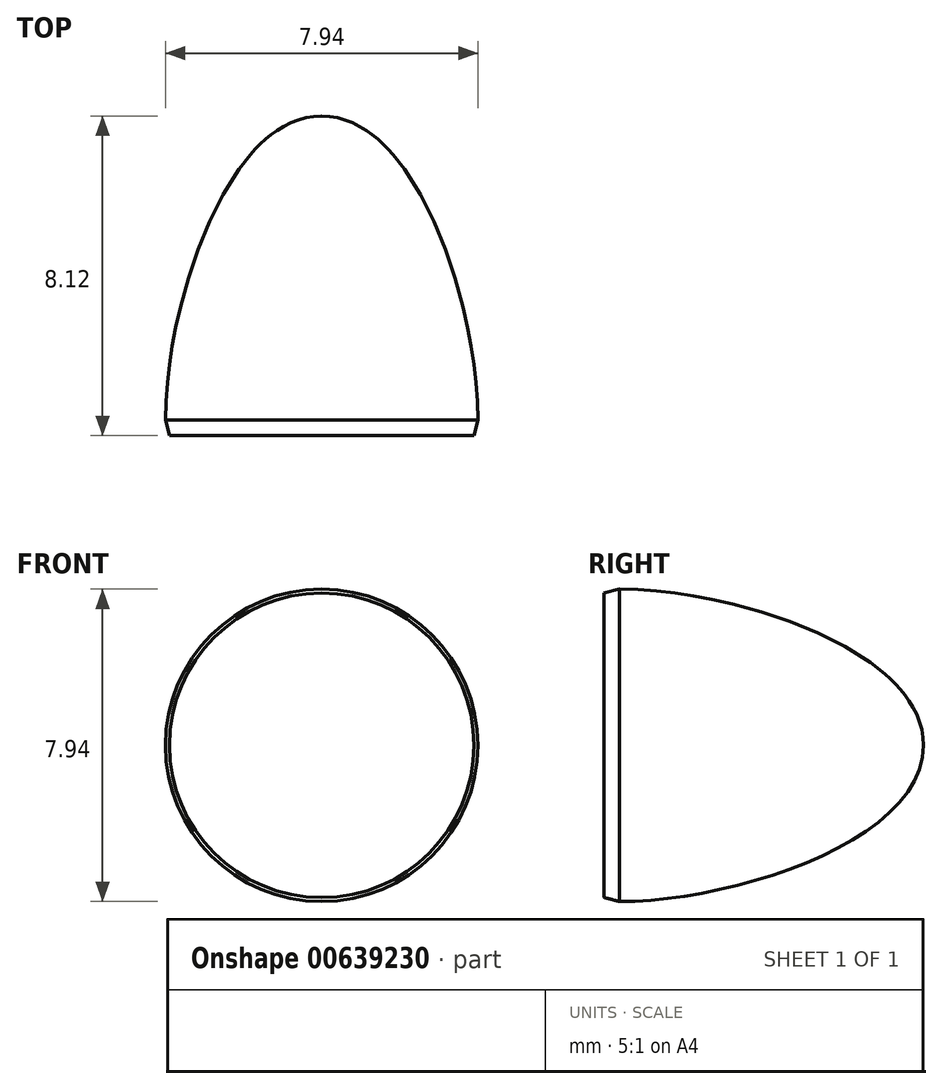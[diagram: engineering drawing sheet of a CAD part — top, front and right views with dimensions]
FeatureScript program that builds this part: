
annotation { "Feature Type Name" : "Feature", "Feature Type Description" : "" }
export const myFeature = defineFeature(function(context is Context, id is Id, definition is map)
    precondition{}
    {
        {
            var Q0;
            Q0=qCreatedBy(makeId("Right.planeOp"),FACE);
            var sketch = newSketch(context, id + "F0", { "sketchPlane" : qUnion([Q0])});
            skLineSegment(sketch, "E0", {"start": v(-7.46, 0) * mm, "end": v(7.72, 0) * mm, "construction": true});
            skLineSegment(sketch, "E1", {"start": v(0, 0) * mm, "end": v(0, -3.87) * mm, "construction": true});
            skPoint(sketch, "E2.orphan", {"position": v(0, 5.07) * mm});
            skFitSpline(sketch, "E3", {"points": [v(0, -3.97) * mm, v(7.72, 0) * mm], "startDerivative": vector(8.68, 0) * mm, "endDerivative": vector(0, 7.29) * mm});
            skLineSegment(sketch, "E4", {"start": v(7.72, 0) * mm, "end": v(7.72, 4.51) * mm, "construction": true});
            skLineSegment(sketch, "E5", {"start": v(0, -3.97) * mm, "end": v(-9.45, -3.97) * mm, "construction": true});
            skLineSegment(sketch, "E6", {"start": v(-0.4, -3.87) * mm, "end": v(-0.4, 0) * mm});
            skLineSegment(sketch, "E7", {"start": v(-0.4, 0) * mm, "end": v(7.72, 0) * mm});
            skLineSegment(sketch, "E8", {"start": v(0, -3.97) * mm, "end": v(-0.4, -3.87) * mm});
            skSolve(sketch);
        }
        {
            var Q0;
            Q0=makeQuery(id+"F0.imprint","IMPRINT",FACE,{"disambiguationData":[TD([[makeQuery(id+"F0.imprint","IMPRINT",EDGE,{"derivedFrom":sQuery(id+"F0.wireOp",EDGE,"E3")}),1.0]])]});
            var Q1;
            Q1=sQuery(id+"F0.wireOp",EDGE,"E0");
            revolve(context, id + "F1", {"entities" : qUnion([Q0]), "axis" : qUnion([Q1]), "revolveType" : RevolveType.FULL});
        }
    });
